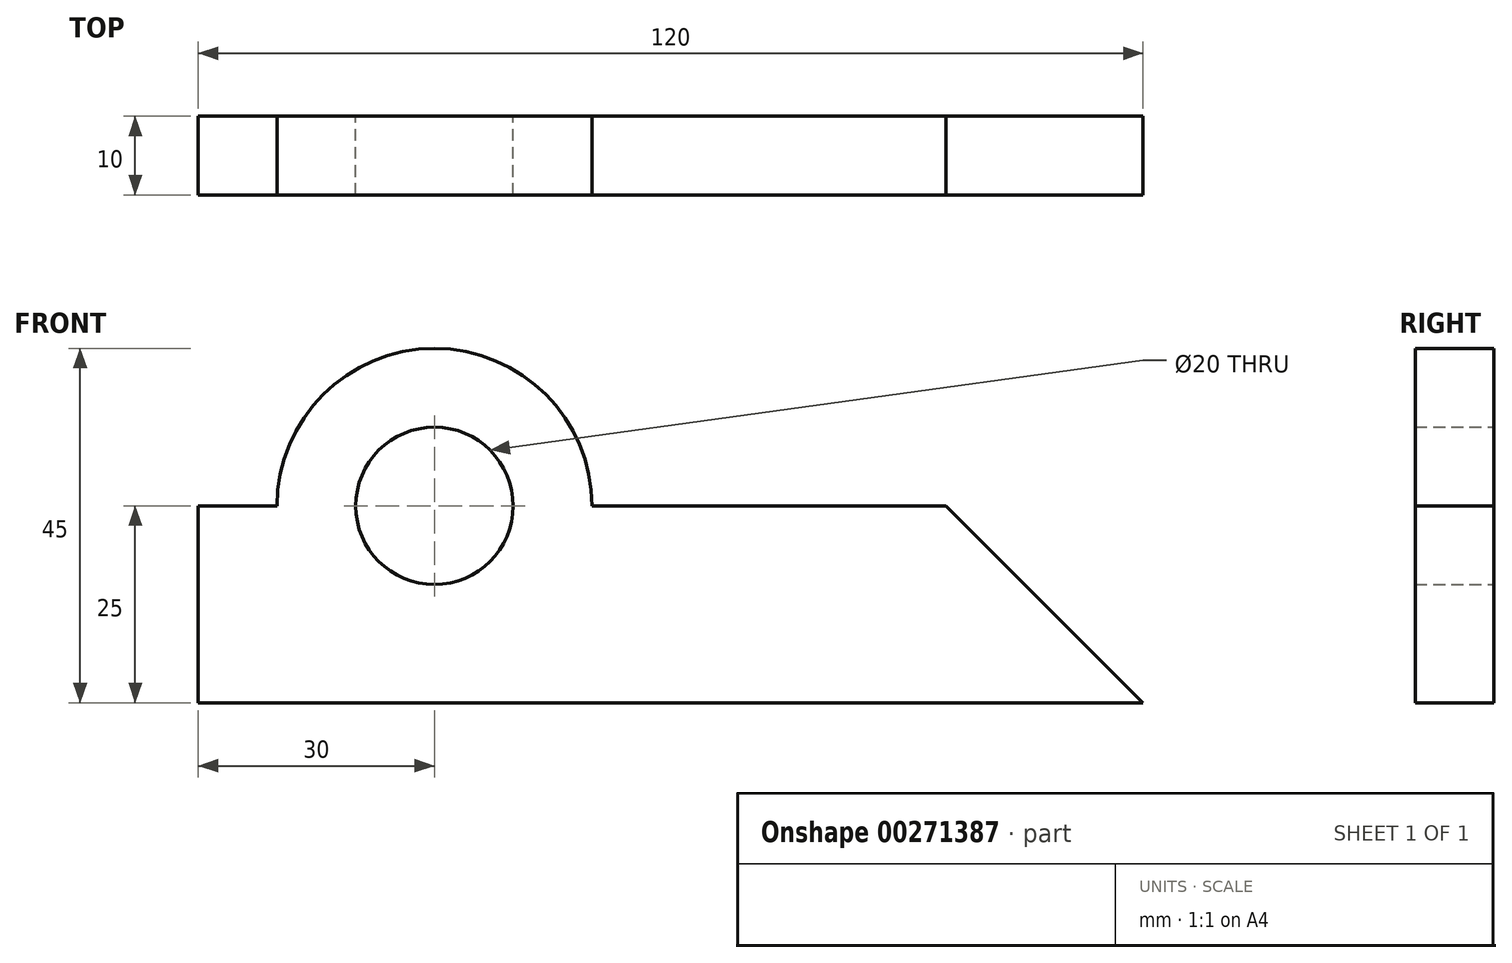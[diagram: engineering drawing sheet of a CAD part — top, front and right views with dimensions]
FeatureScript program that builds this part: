
annotation { "Feature Type Name" : "Feature", "Feature Type Description" : "" }
export const myFeature = defineFeature(function(context is Context, id is Id, definition is map)
    precondition{}
    {
        {
            var Q0;
            Q0=qCreatedBy(makeId("Front.planeOp"),FACE);
            var sketch = newSketch(context, id + "F0", { "sketchPlane" : qUnion([Q0])});
            skLineSegment(sketch, "E0", {"start": v(0, 0) * mm, "end": v(120, 0) * mm});
            skLineSegment(sketch, "E1", {"start": v(120, 0) * mm, "end": v(95, 25) * mm});
            skLineSegment(sketch, "E2", {"start": v(0, 0) * mm, "end": v(0, 25) * mm});
            skLineSegment(sketch, "E3", {"start": v(0, 25) * mm, "end": v(10, 25) * mm});
            skCircle(sketch, "E4", {"center": v(30, 25) * mm, "radius": 10 * mm});
            skLineSegment(sketch, "E5", {"start": v(95, 25) * mm, "end": v(50, 25) * mm});
            skArc(sketch, "E6", {"start": v(50, 25) * mm, "mid": v(30, 45) * mm, "end": v(10, 25) * mm});
            skSolve(sketch);
        }
        {
            var Q0;
            Q0 = qSketchRegion(id + "F0", true);
            extrude(context, id + "F1", {"entities" : qUnion([Q0]), "depth" : 10 * mm});
        }
    });
